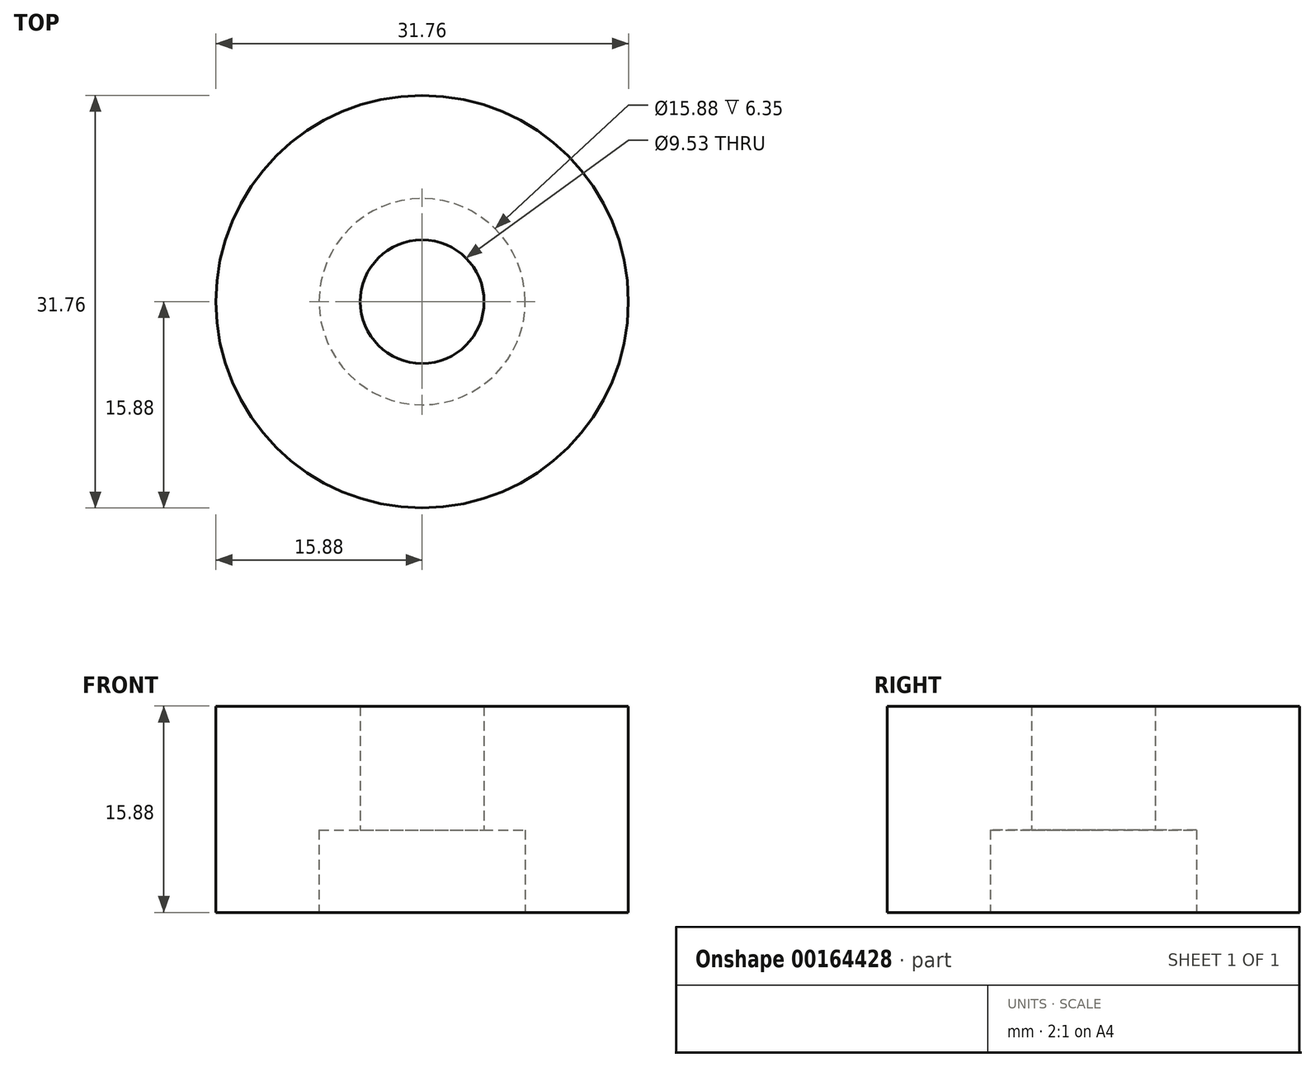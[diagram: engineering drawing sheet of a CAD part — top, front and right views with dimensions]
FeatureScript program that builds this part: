
annotation { "Feature Type Name" : "Feature", "Feature Type Description" : "" }
export const myFeature = defineFeature(function(context is Context, id is Id, definition is map)
    precondition{}
    {
        {
            var Q0;
            Q0=qCreatedBy(makeId("Top.planeOp"),FACE);
            var sketch = newSketch(context, id + "F0", { "sketchPlane" : qUnion([Q0])});
            skCircle(sketch, "E0", {"center": v(0, 0) * mm, "radius": 15.88 * mm});
            skCircle(sketch, "E1", {"center": v(0, 0) * mm, "radius": 7.94 * mm});
            skSolve(sketch);
        }
        {
            var Q0;
            Q0=makeQuery(id+"F0.imprint","IMPRINT",FACE,{"disambiguationData":[TD([[makeQuery(id+"F0.imprint","IMPRINT",EDGE,{"derivedFrom":sQuery(id+"F0.wireOp",EDGE,"E0")}),1.0]])]});
            var Q1;
            Q1=makeQuery(id+"F0.imprint","IMPRINT",FACE,{"disambiguationData":[TD([[makeQuery(id+"F0.imprint","IMPRINT",EDGE,{"derivedFrom":sQuery(id+"F0.wireOp",EDGE,"E1")}),1.0]])]});
            extrude(context, id + "F1", {"entities" : qUnion([Q0, Q1]), "depth" : 15.88 * mm});
        }
        {
            var Q0;
            Q0=makeQuery(id+"F1.opExtrude","CAP_FACE",FACE,{"disambiguationData":[OSD([sQuery(id+"F0.wireOp",EDGE,"E0")])],"isStart":true});
            var sketch = newSketch(context, id + "F2", { "sketchPlane" : qUnion([Q0])});
            skCircle(sketch, "E2", {"center": v(0, 0) * mm, "radius": 7.94 * mm});
            skSolve(sketch);
        }
        {
            var Q0;
            Q0 = qSketchRegion(id + "F2", true);
            extrude(context, id + "F3", {"entities" : qUnion([Q0]), "operationType" : NewBodyOperationType.REMOVE, "oppositeDirection" : true, "depth" : 6.35 * mm});
        }
        {
            var Q0;
            Q0=makeQuery(id+"F3.boolean.opBoolean","COPY",FACE,{"derivedFrom":makeQuery(id+"F3.opExtrude","CAP_FACE",FACE,{"disambiguationData":[OSD([sQuery(id+"F2.wireOp",EDGE,"E2")])],"isStart":false})});
            var sketch = newSketch(context, id + "F4", { "sketchPlane" : qUnion([Q0])});
            skCircle(sketch, "E3", {"center": v(0, 0) * mm, "radius": 4.76 * mm});
            skSolve(sketch);
        }
        {
            var Q0;
            Q0 = qSketchRegion(id + "F4", true);
            extrude(context, id + "F5", {"entities" : qUnion([Q0]), "operationType" : NewBodyOperationType.REMOVE, "oppositeDirection" : true, "depth" : 25.4 * mm});
        }
    });
